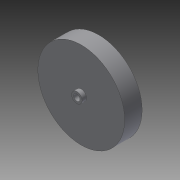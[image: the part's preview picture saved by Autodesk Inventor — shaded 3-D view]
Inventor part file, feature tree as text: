
AUTODESK INVENTOR PART (.ipt)
format: ipt  version: 2014 SP1 (Build 180222100, 222)  size: 82,432 bytes
history: native  units: in
note: dims shown in document units (in); Inventor stores cm internally (conversion verified against a paired STEP export)
features: other x3, sketch x1
ambient origin geometry x8: Origin, YZ Plane, XZ Plane, XY Plane, X Axis, Y Axis, Z Axis, Center Point
bodies: Solid1 (feature_tree)
feature tree (4):
  other  "Front Wheel.ipt"
  other  "Solid1::Front Wheel.ipt"
  other  "TaggingFeature1"
  sketch  "Sketch1"  dims[d0=0.3937in d1=0.3in d2=0.5in d3=0.83in d4=0.0in d5=1.25in d6=0.0in]
